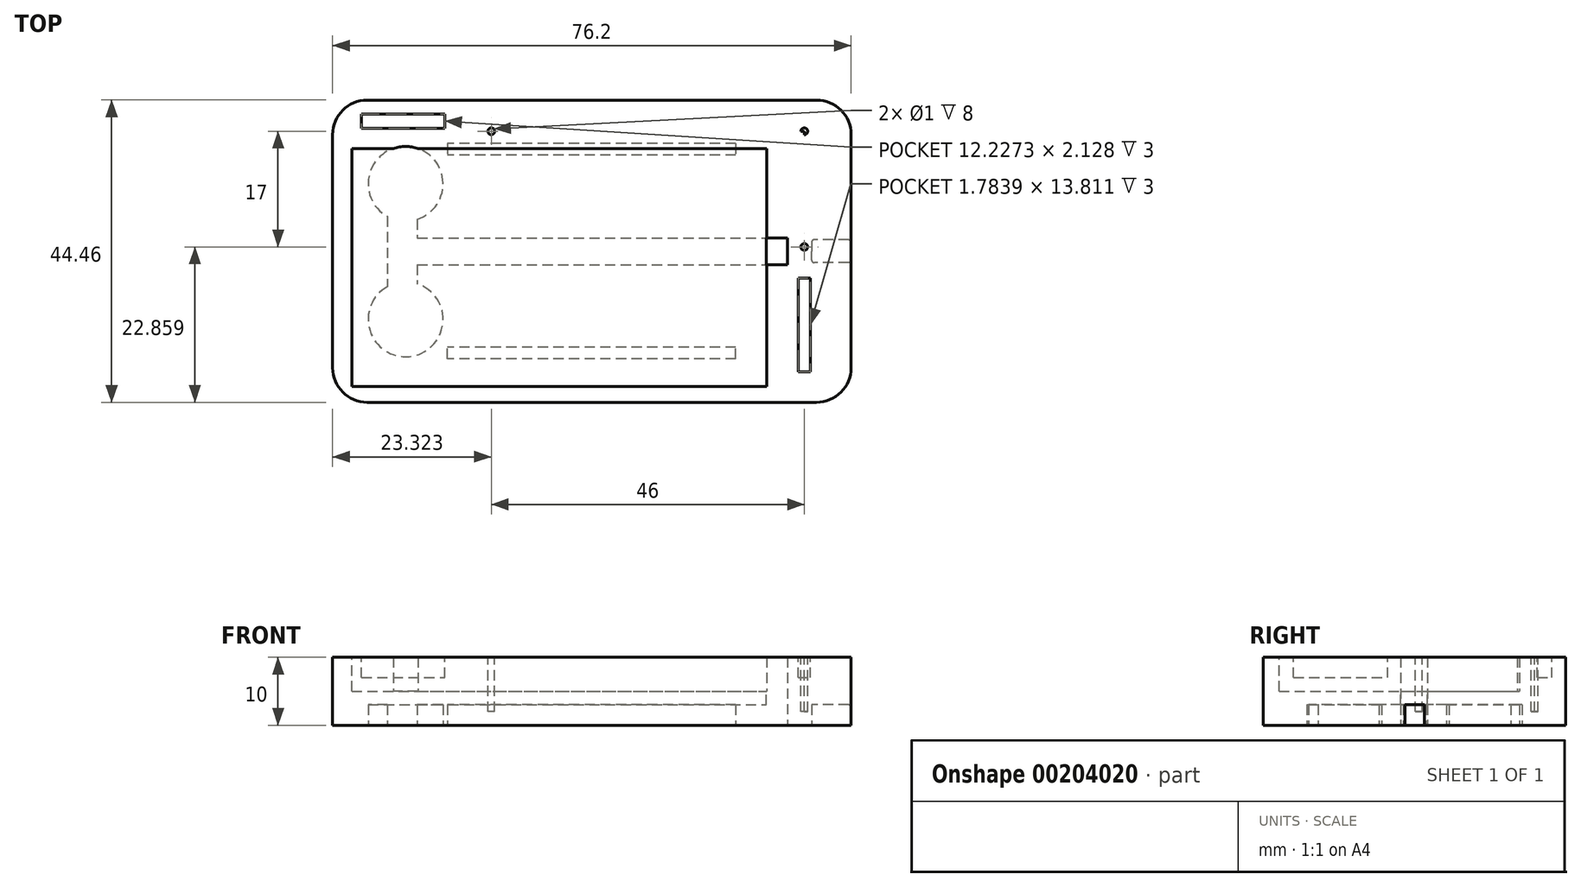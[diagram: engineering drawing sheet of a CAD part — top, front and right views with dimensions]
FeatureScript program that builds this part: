
annotation { "Feature Type Name" : "Feature", "Feature Type Description" : "" }
export const myFeature = defineFeature(function(context is Context, id is Id, definition is map)
    precondition{}
    {
        {
            var Q0;
            Q0=qCreatedBy(makeId("Top.planeOp"),FACE);
            var sketch = newSketch(context, id + "F0", { "sketchPlane" : qUnion([Q0])});
            skLineSegment(sketch, "E0.bottom", {"start": v(38.1, 22.22) * mm, "end": v(-38.1, 22.22) * mm});
            skLineSegment(sketch, "E0.top", {"start": v(38.1, -22.22) * mm, "end": v(-38.1, -22.22) * mm});
            skLineSegment(sketch, "E0.left", {"start": v(38.1, 22.22) * mm, "end": v(38.1, -22.22) * mm});
            skLineSegment(sketch, "E0.right", {"start": v(-38.1, 22.22) * mm, "end": v(-38.1, -22.23) * mm});
            skPoint(sketch, "E0.middle", {"position": v(0, 0) * mm});
            skLineSegment(sketch, "E1", {"start": v(-27.37, 9.9) * mm, "end": v(-27.37, -10.03) * mm});
            skCircle(sketch, "E2", {"center": v(-27.37, 9.9) * mm, "radius": 5.5 * mm});
            skCircle(sketch, "E3", {"center": v(-27.37, -10.03) * mm, "radius": 5.5 * mm});
            skLineSegment(sketch, "E4", {"start": v(-25.66, 4.67) * mm, "end": v(-25.66, -4.8) * mm});
            skLineSegment(sketch, "E5", {"start": v(-30.05, 5.1) * mm, "end": v(-30.05, -5.23) * mm});
            skLineSegment(sketch, "E6", {"start": v(-25.66, 1.93) * mm, "end": v(26.37, 1.93) * mm});
            skLineSegment(sketch, "E7", {"start": v(-25.66, -2) * mm, "end": v(26.37, -2) * mm});
            skLineSegment(sketch, "E8", {"start": v(26.37, -2) * mm, "end": v(28.74, -2) * mm});
            skLineSegment(sketch, "E9", {"start": v(26.37, 1.93) * mm, "end": v(28.74, 1.93) * mm});
            skLineSegment(sketch, "E10", {"start": v(28.74, -2) * mm, "end": v(28.74, 1.93) * mm});
            skPoint(sketch, "E10.endSnap0", {"position": v(28.08, 1.93) * mm});
            skPoint(sketch, "E11.orphan", {"position": v(29.8, 1.93) * mm});
            skSolve(sketch);
        }
        {
            var Q0;
            Q0=makeQuery(id+"F0.imprint","IMPRINT",FACE,{"disambiguationData":[TD([[makeQuery(id+"F0.imprint","IMPRINT",EDGE,{"derivedFrom":sQuery(id+"F0.wireOp",EDGE,"E0.bottom")}),1.0]])]});
            extrude(context, id + "F1", {"entities" : qUnion([Q0]), "depth" : 10 * mm});
        }
        {
            var Q0;
            Q0=makeQuery(id+"F1.opExtrude","CAP_FACE",FACE,{"disambiguationData":[OSD([sQuery(id+"F0.wireOp",EDGE,"E0.bottom"),sQuery(id+"F0.wireOp",EDGE,"E0.top"),sQuery(id+"F0.wireOp",EDGE,"E0.left"),sQuery(id+"F0.wireOp",EDGE,"E0.right")])],"isStart":false});
            var sketch = newSketch(context, id + "F2", { "sketchPlane" : qUnion([Q0])});
            skSolve(sketch);
        }
        {
            var Q0;
            Q0=makeQuery(id+"F2.imprint","IMPRINT",FACE,{"disambiguationData":[TD([[makeQuery(id+"F2.imprint","IMPRINT",EDGE,{"derivedFrom":makeQuery(id+"F1.opExtrude","CAP_EDGE",EDGE,{"disambiguationData":[OSD([sQuery(id+"F0.wireOp",EDGE,"E0.bottom")])],"isStart":false})}),1.0]])]});
            var sketch = newSketch(context, id + "F3", { "sketchPlane" : qUnion([Q0])});
            skLineSegment(sketch, "E12.bottom", {"start": v(-35.3, -19.9) * mm, "end": v(25.67, -19.9) * mm});
            skLineSegment(sketch, "E12.top", {"start": v(-35.3, 15.1) * mm, "end": v(25.67, 15.1) * mm});
            skLineSegment(sketch, "E12.left", {"start": v(-35.3, -19.9) * mm, "end": v(-35.3, 15.1) * mm});
            skLineSegment(sketch, "E12.right", {"start": v(25.67, -19.9) * mm, "end": v(25.67, 15.1) * mm});
            skSolve(sketch);
        }
        {
            var Q0;
            Q0=makeQuery(id+"F2.imprint","IMPRINT",FACE,{"disambiguationData":[TD([[makeQuery(id+"F2.imprint","IMPRINT",EDGE,{"derivedFrom":makeQuery(id+"F1.opExtrude","CAP_EDGE",EDGE,{"disambiguationData":[OSD([sQuery(id+"F0.wireOp",EDGE,"E0.bottom")])],"isStart":false})}),1.0]])]});
            var sketch = newSketch(context, id + "F4", { "sketchPlane" : qUnion([Q0])});
            skLineSegment(sketch, "E13", {"start": v(31.22, 17.63) * mm, "end": v(31.22, 0.63) * mm});
            skCircle(sketch, "E14", {"center": v(31.22, 17.63) * mm, "radius": 0.5 * mm});
            skCircle(sketch, "E15", {"center": v(31.22, 0.63) * mm, "radius": 0.5 * mm});
            skLineSegment(sketch, "E16", {"start": v(31.22, 17.63) * mm, "end": v(-14.78, 17.63) * mm});
            skCircle(sketch, "E17", {"center": v(-14.78, 17.63) * mm, "radius": 0.5 * mm});
            skSolve(sketch);
        }
        {
            var Q0;
            Q0 = qSketchRegion(id + "F3", true);
            extrude(context, id + "F5", {"entities" : qUnion([Q0]), "operationType" : NewBodyOperationType.REMOVE, "oppositeDirection" : true, "depth" : 5 * mm});
        }
        {
            var Q0;
            Q0=makeQuery(id+"F0.imprint","IMPRINT",FACE,{"disambiguationData":[TD([[makeQuery(id+"F0.imprint","IMPRINT",EDGE,{"derivedFrom":sQuery(id+"F0.wireOp",EDGE,"E2")}),1.0]])]});
            var Q1;
            Q1=makeQuery(id+"F0.imprint","IMPRINT",FACE,{"disambiguationData":[TD([[makeQuery(id+"F0.imprint","IMPRINT",EDGE,{"derivedFrom":sQuery(id+"F0.wireOp",EDGE,"E3")}),1.0]])]});
            var Q2;
            Q2=sQuery(id+"F0.wireOp",EDGE,"E2");
            var Q3;
            Q3=sQuery(id+"F0.wireOp",EDGE,"E3");
            extrude(context, id + "F6", {"entities" : qUnion([Q0, Q1]), "operationType" : NewBodyOperationType.REMOVE, "surfaceEntities" : qUnion([Q2, Q3]), "depth" : 3 * mm});
        }
        {
            var Q0;
            {var subQ1=sQuery(id+"F0.wireOp",EDGE,"E6");Q0=makeQuery(id+"F0.imprint","IMPRINT",FACE,{"disambiguationData":[TD([[makeQuery(id+"F0.imprint","IMPRINT",EDGE,{"derivedFrom":subQ1}),-1.0]])]});}
            var Q1;
            {var subQ0=sQuery(id+"F0.wireOp",EDGE,"E3");var subQ1=makeQuery(id+"F0.imprint","INTERSECT",VERTEX,{"derivedFrom":[subQ0,sQuery(id+"F0.wireOp",EDGE,"E4")]});Q1=makeQuery(id+"F0.imprint","IMPRINT",FACE,{"disambiguationData":[TD([[makeQuery(id+"F0.imprint","IMPRINT",EDGE,{"disambiguationData":[TD([[subQ1,-1.0]])],"derivedFrom":subQ0}),1.0]])]});}
            var Q2;
            {var subQ5=sQuery(id+"F0.wireOp",EDGE,"E5");Q2=makeQuery(id+"F0.imprint","IMPRINT",FACE,{"disambiguationData":[TD([[makeQuery(id+"F0.imprint","IMPRINT",EDGE,{"derivedFrom":subQ5}),1.0]])]});}
            var Q3;
            {var subQ0=sQuery(id+"F0.wireOp",EDGE,"E2");var subQ1=makeQuery(id+"F0.imprint","INTERSECT",VERTEX,{"derivedFrom":[subQ0,sQuery(id+"F0.wireOp",EDGE,"E5")]});Q3=makeQuery(id+"F0.imprint","IMPRINT",FACE,{"disambiguationData":[TD([[makeQuery(id+"F0.imprint","IMPRINT",EDGE,{"disambiguationData":[TD([[subQ1,-1.0]])],"derivedFrom":subQ0}),1.0]])]});}
            var Q4;
            {var subQ1=sQuery(id+"F0.wireOp",EDGE,"E2");var subQ6=sQuery(id+"F0.wireOp",EDGE,"E1");var subQ8=makeQuery(id+"F0.imprint","INTERSECT",VERTEX,{"derivedFrom":[subQ6,subQ1]});Q4=makeQuery(id+"F0.imprint","IMPRINT",FACE,{"disambiguationData":[TD([[makeQuery(id+"F0.imprint","IMPRINT",EDGE,{"disambiguationData":[TD([[subQ8,-1.0]])],"derivedFrom":subQ6}),1.0]])]});}
            extrude(context, id + "F7", {"entities" : qUnion([Q0, Q1, Q2, Q3, Q4]), "operationType" : NewBodyOperationType.ADD, "depth" : 5 * mm});
        }
        {
            var Q0;
            {var subQ1=sQuery(id+"F0.wireOp",EDGE,"E6");Q0=makeQuery(id+"F0.imprint","IMPRINT",FACE,{"disambiguationData":[TD([[makeQuery(id+"F0.imprint","IMPRINT",EDGE,{"derivedFrom":subQ1}),-1.0]])]});}
            var Q1;
            {var subQ0=sQuery(id+"F0.wireOp",EDGE,"E2");var subQ1=makeQuery(id+"F0.imprint","INTERSECT",VERTEX,{"derivedFrom":[subQ0,sQuery(id+"F0.wireOp",EDGE,"E5")]});Q1=makeQuery(id+"F0.imprint","IMPRINT",FACE,{"disambiguationData":[TD([[makeQuery(id+"F0.imprint","IMPRINT",EDGE,{"disambiguationData":[TD([[subQ1,-1.0]])],"derivedFrom":subQ0}),1.0]])]});}
            var Q2;
            {var subQ5=sQuery(id+"F0.wireOp",EDGE,"E5");Q2=makeQuery(id+"F0.imprint","IMPRINT",FACE,{"disambiguationData":[TD([[makeQuery(id+"F0.imprint","IMPRINT",EDGE,{"derivedFrom":subQ5}),1.0]])]});}
            var Q3;
            {var subQ1=sQuery(id+"F0.wireOp",EDGE,"E2");var subQ6=sQuery(id+"F0.wireOp",EDGE,"E1");var subQ8=makeQuery(id+"F0.imprint","INTERSECT",VERTEX,{"derivedFrom":[subQ6,subQ1]});Q3=makeQuery(id+"F0.imprint","IMPRINT",FACE,{"disambiguationData":[TD([[makeQuery(id+"F0.imprint","IMPRINT",EDGE,{"disambiguationData":[TD([[subQ8,-1.0]])],"derivedFrom":subQ6}),1.0]])]});}
            var Q4;
            {var subQ0=sQuery(id+"F0.wireOp",EDGE,"E3");var subQ1=makeQuery(id+"F0.imprint","INTERSECT",VERTEX,{"derivedFrom":[subQ0,sQuery(id+"F0.wireOp",EDGE,"E4")]});Q4=makeQuery(id+"F0.imprint","IMPRINT",FACE,{"disambiguationData":[TD([[makeQuery(id+"F0.imprint","IMPRINT",EDGE,{"disambiguationData":[TD([[subQ1,-1.0]])],"derivedFrom":subQ0}),1.0]])]});}
            extrude(context, id + "F8", {"entities" : qUnion([Q0, Q1, Q2, Q3, Q4]), "operationType" : NewBodyOperationType.REMOVE, "depth" : 3 * mm});
        }
        {
            var Q0;
            Q0=makeQuery(id+"F1.opExtrude","SWEPT_EDGE",EDGE,{"disambiguationData":[OSD([sQuery(id+"F0.wireOp",EDGE,"E0.bottom"),sQuery(id+"F0.wireOp",EDGE,"E0.left")])]});
            var Q1;
            Q1=makeQuery(id+"F1.opExtrude","SWEPT_EDGE",EDGE,{"disambiguationData":[OSD([sQuery(id+"F0.wireOp",EDGE,"E0.top"),sQuery(id+"F0.wireOp",EDGE,"E0.left")])]});
            var Q2;
            Q2=makeQuery(id+"F1.opExtrude","SWEPT_EDGE",EDGE,{"disambiguationData":[OSD([sQuery(id+"F0.wireOp",EDGE,"E0.top"),sQuery(id+"F0.wireOp",EDGE,"E0.right")])]});
            var Q3;
            Q3=makeQuery(id+"F1.opExtrude","SWEPT_EDGE",EDGE,{"disambiguationData":[OSD([sQuery(id+"F0.wireOp",EDGE,"E0.bottom"),sQuery(id+"F0.wireOp",EDGE,"E0.right")])]});
            fillet(context, id + "F9", {"entities" : qUnion([Q0, Q1, Q2, Q3]), "radius" : 5.08 * mm, "tangentPropagation" : true, "allowEdgeOverflow" : false});
        }
        {
            var Q0;
            Q0=makeQuery(id+"F2.imprint","IMPRINT",FACE,{"disambiguationData":[TD([[makeQuery(id+"F2.imprint","IMPRINT",EDGE,{"derivedFrom":makeQuery(id+"F1.opExtrude","CAP_EDGE",EDGE,{"disambiguationData":[OSD([sQuery(id+"F0.wireOp",EDGE,"E0.bottom")])],"isStart":false})}),1.0]])]});
            var sketch = newSketch(context, id + "F10", { "sketchPlane" : qUnion([Q0])});
            skLineSegment(sketch, "E18", {"start": v(25.64, -2.02) * mm, "end": v(25.64, 1.97) * mm});
            skSolve(sketch);
        }
        {
            var Q0;
            {var subQ5=makeQuery(id+"F2.imprint","IMPRINT",EDGE,{"derivedFrom":makeQuery(id+"F1.opExtrude","CAP_EDGE",EDGE,{"disambiguationData":[OSD([sQuery(id+"F0.wireOp",EDGE,"E10")])],"isStart":false})});Q0=makeQuery(id+"F10.imprint","IMPRINT",FACE,{"disambiguationData":[TD([[makeQuery(id+"F10.imprint","IMPRINT",EDGE,{"derivedFrom":subQ5}),1.0]])]});}
            extrude(context, id + "F11", {"entities" : qUnion([Q0]), "operationType" : NewBodyOperationType.REMOVE, "oppositeDirection" : true, "depth" : 11 * mm});
        }
        {
            var Q0;
            Q0=makeQuery(id+"F0.imprint","IMPRINT",FACE,{"disambiguationData":[TD([[makeQuery(id+"F0.imprint","IMPRINT",EDGE,{"derivedFrom":sQuery(id+"F0.wireOp",EDGE,"E0.bottom")}),1.0]])]});
            var sketch = newSketch(context, id + "F12", { "sketchPlane" : qUnion([Q0])});
            skLineSegment(sketch, "E19.bottom", {"start": v(21.14, -15.83) * mm, "end": v(-21.22, -15.83) * mm});
            skLineSegment(sketch, "E19.top", {"start": v(21.14, -14.16) * mm, "end": v(-21.22, -14.16) * mm});
            skLineSegment(sketch, "E19.left", {"start": v(21.14, -15.83) * mm, "end": v(21.14, -14.16) * mm});
            skLineSegment(sketch, "E19.right", {"start": v(-21.22, -15.83) * mm, "end": v(-21.22, -14.16) * mm});
            skLineSegment(sketch, "E20.MirrorCS", {"start": v(21.14, 14.16) * mm, "end": v(-21.22, 14.16) * mm});
            skLineSegment(sketch, "E21.MirrorCS", {"start": v(21.14, 15.83) * mm, "end": v(-21.22, 15.83) * mm});
            skLineSegment(sketch, "E22.MirrorCS", {"start": v(21.14, 15.83) * mm, "end": v(21.14, 14.16) * mm});
            skLineSegment(sketch, "E23.MirrorCS", {"start": v(-21.22, 15.83) * mm, "end": v(-21.22, 14.16) * mm});
            skSolve(sketch);
        }
        {
            var Q0;
            Q0 = qSketchRegion(id + "F12", true);
            extrude(context, id + "F13", {"entities" : qUnion([Q0]), "operationType" : NewBodyOperationType.REMOVE, "depth" : 3 * mm});
        }
        {
            var Q0;
            Q0=makeQuery(id+"F4.imprint","IMPRINT",FACE,{"disambiguationData":[TD([[makeQuery(id+"F4.imprint","IMPRINT",EDGE,{"derivedFrom":sQuery(id+"F4.wireOp",EDGE,"E17")}),1.0]])]});
            var Q1;
            {var subQ0=sQuery(id+"F4.wireOp",EDGE,"E16");var subQ1=sQuery(id+"F4.wireOp",EDGE,"E13");var subQ2=makeQuery(id+"F4.imprint","INTERSECT",VERTEX,{"derivedFrom":[subQ1,subQ0]});Q1=makeQuery(id+"F4.imprint","IMPRINT",FACE,{"disambiguationData":[TD([[makeQuery(id+"F4.imprint","IMPRINT",EDGE,{"disambiguationData":[TD([[subQ2,-1.0]])],"derivedFrom":subQ1}),1.0]])]});}
            var Q2;
            Q2=makeQuery(id+"F4.imprint","IMPRINT",FACE,{"disambiguationData":[TD([[makeQuery(id+"F4.imprint","IMPRINT",EDGE,{"derivedFrom":sQuery(id+"F4.wireOp",EDGE,"E15")}),1.0]])]});
            extrude(context, id + "F14", {"entities" : qUnion([Q0, Q1, Q2]), "operationType" : NewBodyOperationType.REMOVE, "oppositeDirection" : true, "depth" : 8 * mm});
        }
        {
            var Q0;
            Q0=makeQuery(id+"F0.imprint","IMPRINT",FACE,{"disambiguationData":[TD([[makeQuery(id+"F0.imprint","IMPRINT",EDGE,{"derivedFrom":sQuery(id+"F0.wireOp",EDGE,"E0.bottom")}),1.0]])]});
            var sketch = newSketch(context, id + "F15", { "sketchPlane" : qUnion([Q0])});
            skLineSegment(sketch, "E24.bottom", {"start": v(37.76, -1.65) * mm, "end": v(32.67, -1.68) * mm});
            skLineSegment(sketch, "E24.left", {"start": v(38.13, -1.28) * mm, "end": v(38.13, 0) * mm});
            skLineSegment(sketch, "E24.right", {"start": v(32.3, -1.31) * mm, "end": v(32.3, 0) * mm});
            skLineSegment(sketch, "E25.MirrorCS", {"start": v(38.13, 1.28) * mm, "end": v(38.13, 0) * mm});
            skLineSegment(sketch, "E26.MirrorCS", {"start": v(32.3, 1.31) * mm, "end": v(32.3, 0) * mm});
            skLineSegment(sketch, "E27.MirrorCS", {"start": v(37.76, 1.65) * mm, "end": v(32.67, 1.68) * mm});
            skPoint(sketch, "E28.MirrorCS.end.orphan", {"position": v(32.3, 0) * mm});
            skPoint(sketch, "E28.MirrorCS.start.orphan", {"position": v(38.13, 0) * mm});
            skPoint(sketch, "E29.visualSharp", {"position": v(32.3, 1.68) * mm});
            skArc(sketch, "E29.filletArc", {"start": v(32.67, 1.68) * mm, "mid": v(32.41, 1.57) * mm, "end": v(32.3, 1.31) * mm});
            skPoint(sketch, "E30.visualSharp", {"position": v(32.3, -1.68) * mm});
            skArc(sketch, "E30.filletArc", {"start": v(32.3, -1.31) * mm, "mid": v(32.41, -1.57) * mm, "end": v(32.67, -1.68) * mm});
            skPoint(sketch, "E31.visualSharp", {"position": v(38.13, -1.65) * mm});
            skArc(sketch, "E31.filletArc", {"start": v(37.76, -1.65) * mm, "mid": v(38.02, -1.55) * mm, "end": v(38.13, -1.28) * mm});
            skPoint(sketch, "E32.visualSharp", {"position": v(38.13, 1.65) * mm});
            skArc(sketch, "E32.filletArc", {"start": v(38.13, 1.28) * mm, "mid": v(38.02, 1.55) * mm, "end": v(37.76, 1.65) * mm});
            skSolve(sketch);
        }
        {
            var Q0;
            {var subQ1=sQuery(id+"F15.wireOp",EDGE,"E24.bottom");Q0=makeQuery(id+"F15.imprint","IMPRINT",FACE,{"disambiguationData":[TD([[makeQuery(id+"F15.imprint","IMPRINT",EDGE,{"derivedFrom":subQ1}),-1.0]])]});}
            extrude(context, id + "F16", {"entities" : qUnion([Q0]), "operationType" : NewBodyOperationType.REMOVE, "depth" : 3 * mm});
        }
        {
            var Q0;
            Q0=makeQuery(id+"F10.imprint","IMPRINT",FACE,{"disambiguationData":[TD([[makeQuery(id+"F10.imprint","IMPRINT",EDGE,{"derivedFrom":makeQuery(id+"F2.imprint","IMPRINT",EDGE,{"derivedFrom":makeQuery(id+"F1.opExtrude","CAP_EDGE",EDGE,{"disambiguationData":[OSD([sQuery(id+"F0.wireOp",EDGE,"E0.bottom")])],"isStart":false})})}),1.0]])]});
            var sketch = newSketch(context, id + "F17", { "sketchPlane" : qUnion([Q0])});
            skLineSegment(sketch, "E33.bottom", {"start": v(30.32, -17.77) * mm, "end": v(32.1, -17.77) * mm});
            skLineSegment(sketch, "E33.top", {"start": v(30.32, -3.96) * mm, "end": v(32.1, -3.96) * mm});
            skLineSegment(sketch, "E33.left", {"start": v(30.32, -17.77) * mm, "end": v(30.32, -3.96) * mm});
            skLineSegment(sketch, "E33.right", {"start": v(32.1, -17.77) * mm, "end": v(32.1, -3.96) * mm});
            skLineSegment(sketch, "E34.bottom", {"start": v(-33.84, 18.05) * mm, "end": v(-21.61, 18.05) * mm});
            skLineSegment(sketch, "E34.top", {"start": v(-33.84, 20.18) * mm, "end": v(-21.61, 20.18) * mm});
            skLineSegment(sketch, "E34.left", {"start": v(-33.84, 18.05) * mm, "end": v(-33.84, 20.18) * mm});
            skLineSegment(sketch, "E34.right", {"start": v(-21.61, 18.05) * mm, "end": v(-21.61, 20.18) * mm});
            skSolve(sketch);
        }
        {
            var Q0;
            Q0=makeQuery(id+"F17.imprint","IMPRINT",FACE,{"disambiguationData":[TD([[makeQuery(id+"F17.imprint","IMPRINT",EDGE,{"derivedFrom":sQuery(id+"F17.wireOp",EDGE,"E33.bottom")}),1.0]])]});
            var Q1;
            Q1=makeQuery(id+"F17.imprint","IMPRINT",FACE,{"disambiguationData":[TD([[makeQuery(id+"F17.imprint","IMPRINT",EDGE,{"derivedFrom":sQuery(id+"F17.wireOp",EDGE,"E34.bottom")}),1.0]])]});
            extrude(context, id + "F18", {"entities" : qUnion([Q0, Q1]), "operationType" : NewBodyOperationType.REMOVE, "oppositeDirection" : true, "depth" : 3 * mm});
        }
    });
